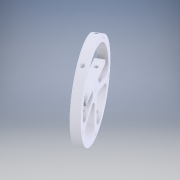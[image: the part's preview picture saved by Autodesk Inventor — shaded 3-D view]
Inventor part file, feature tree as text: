
AUTODESK INVENTOR PART (.ipt)
format: ipt  version: 2017 (Build 210142000, 142)  size: 480,256 bytes
history: native  units: in
note: dims shown in document units (in); Inventor stores cm internally (conversion verified against a paired STEP export)
features: extrude x14, sketch x14, projected_geometry x9, plane x1, imported_body x1
ambient origin geometry x8: Origin, YZ Plane, XZ Plane, XY Plane, X Axis, Y Axis, Z Axis, Center Point
bodies: Solid1 (feature_tree)
feature tree (39):
  extrude  "Extrusion1"  Depth=0.3937in TaperAngle=0.0deg
  extrude  "Extrusion2"  Depth=0.375in
  extrude  "Extrusion3"  Depth=0.125in
  extrude  "Extrusion4"  Depth=0.3937in TaperAngle=0.0deg
  extrude  "Extrusion5"  Depth=0.7087in
  plane  "Work Plane1"
  extrude  "Extrusion6"  Depth=0.9154in
  extrude  "Extrusion7"  Depth=0.1969in
  extrude  "Extrusion8"  Depth=1.3091in
  extrude  "Extrusion9"  Depth=0.0787in TaperAngle=0.0deg
  extrude  "Extrusion10"  Depth=0.125in
  extrude  "Extrusion11"  Depth=0.0787in TaperAngle=0.0deg
  extrude  "Extrusion17"  TaperAngle=90.0deg  [1 undecoded]
  extrude  "Extrusion18"  Depth=0.0787in TaperAngle=0.0deg
  extrude  "Extrusion19"  Depth=0.3937in
  sketch  "Sketch1"  dims[d0=1.25in d1=0.0in d2=0.3937in d3=0.0in]
  projected_geometry  "Projected Loop1"
  projected_geometry  "Projected Loop2"
  projected_geometry  "Projected Loop3"
  sketch  "Sketch2"  dims[d4=0.1969in d5=0.0in d6=0.375in]
  sketch  "Sketch3"  dims[d7=0.5in d8=0.125in]
  projected_geometry  "Projected Loop4"
  sketch  "Sketch4"  dims[d9=0.3937in d10=0.0in d11=0.1875in d12=0.0in]
  sketch  "Sketch5"  dims[d13=3.2677in d19=0.7087in]
  projected_geometry  "Projected Loop5"
  sketch  "Sketch8"  dims[d20=0.6102in d21=0.9154in]
  sketch  "Sketch9"  dims[d22=0.6102in d23=0.1969in]
  sketch  "Sketch11"  dims[d24=0.0787in d25=1.3091in]
  sketch  "Sketch13"  dims[d26=0.6693in d27=0.0in d28=0.0787in d29=0.0in]
  projected_geometry  "Projected Loop8"
  sketch  "Sketch14"  dims[d30=0.0787in d31=0.0in d32=0.125in]
  projected_geometry  "Projected Loop9"
  sketch  "Sketch17"  dims[d33=0.0in d34=0.0787in d35=0.0in]
  projected_geometry  "Projected Loop10"
  sketch  "Sketch23"  dims[d36=0.0787in d37=90.0deg]
  sketch  "Sketch24"  dims[d38=0.5118in d39=0.0787in d40=0.0in]
  sketch  "Sketch25"  dims[d41=1.378in d42=0.0in d59=0.213in d60=1.0825in d61=0.118in d62=0.3937in d63=0.0in d64=0.3937in d65=0.0in d66=90.0deg d67=0.256in d68=0.125in d69=1.752in d70=0.125in d71=1.5748in d72=0.0in d73=1.7717in d74=0.0in]
  projected_geometry  "Projected Loop18"
  imported_body  "Base1"
note: 1 required parameter value undecoded (feature->parameter linkage not recoverable at this tier; creation-order binding heuristic only, values carry confidence <= 0.55)
